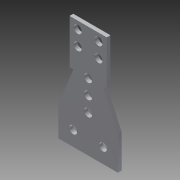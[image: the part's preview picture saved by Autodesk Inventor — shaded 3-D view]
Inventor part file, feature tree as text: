
AUTODESK INVENTOR PART (.ipt)
format: ipt  version: 2013 (Build 170138000, 138)  size: 140,288 bytes
history: native  units: in
note: dims shown in document units (in); Inventor stores cm internally (conversion verified against a paired STEP export)
features: extrude x6, sketch x6, reference x5
ambient origin geometry x8: Origin, YZ Plane, XZ Plane, XY Plane, X Axis, Y Axis, Z Axis, Center Point
bodies: Solid1 (feature_tree)
feature tree (17):
  extrude  "Extrusion1"  Depth=2.25in
  extrude  "Extrusion2"  Depth=0.5in
  extrude  "Extrusion3"  Depth=0.125in TaperAngle=0.0deg
  extrude  "Extrusion4"  Depth=0.125in TaperAngle=0.0deg
  extrude  "Extrusion5"  Depth=0.15in
  extrude  "Extrusion6"  Depth=0.5in
  sketch  "Sketch1"  dims[d0=2.0in d1=2.25in]
  sketch  "Sketch2"  dims[d2=1.0in d3=0.5in]
  sketch  "Sketch3"  dims[d4=0.5in d5=0.125in d6=0.0in]
  reference  "Reference1"
  reference  "Reference2"
  reference  "Reference3"
  reference  "Reference4"
  reference  "Reference5"
  sketch  "Sketch4"  dims[d7=1.5in d8=0.125in d9=0.0in]
  sketch  "Sketch5"  dims[d10=0.125in d11=0.0in d12=0.15in]
  sketch  "Sketch6"  dims[d13=0.25in d14=0.5in d15=0.15in d16=0.266in d17=0.266in d18=0.266in d19=0.266in d20=1.0in d21=0.0in d22=0.125in d23=0.0in d24=0.125in d25=0.0in]
